# Revit family: Sanitary_Accessories_DURAVIT-AG_Starck-T-Toothbrush-cup-65x98x173-mm-009
name_source: partatom
category: Generic Models
revit_build: Autodesk Revit 2018 (Build: 20180329_1100(x64)
units: mm (PartAtom-declared; Revit-internal decimal feet)

## family parameters
Can host rebar = No
Cut with Voids When Loaded = No
Host = Face
OmniClass Number = 23.31.25.00
OmniClass Title = Toilet and Bath Specialties
Part Type = Normal
Room Calculation Point = No
Round Connector Dimension = Use Diameter
Shared = No

## types (2) — shared parameters
BIMobject category = Bathroom Accessories
Default Elevation = 1219 mm
Design country = Germany
ETIM classification = EC010556 | Toothbrush holder
Edition number = 1
IFC Classification = Furnishing Element
Installation instructions = https://pro.duravit.com
Manufacturer = Duravit
Manufacturer country = Germany
Manufacturer name = DURAVIT AG
Masterformat 2014 Code = 01 52 19
Masterformat 2014 Description = Sanitary Facilities
Material main = Brass
Material secondary = Glass frosted
Model = Starck T Toothbrush cup 65x98x173 mm - 009931
OmniClass Code = 23-31 25 00
OmniClass Description = Toilet and Bath Specialties
Product Guid = da395057-32e6-4f7c-89dd-928aacf0623f
Product SKU = Starck-T-Toothbrush-cup-65x98x173-mm-009931
Product certification = https://pro.duravit.com
Product data url = https://bimobject.com
Product family = Starck T
Product group = Toothbrush cup
Product name = Starck T Toothbrush cup 65x98x173 mm - 009931
Product url = https://pro.duravit.com
QR code = https://bimobject.com
Scondary material = Duravit - Glass - Frosted
Technical description = https://pro.duravit.com
UNSPSC Code = 301815
URL = https://www.duravit.com
Uniclass 2015 Code = Pr_40_20
Uniclass 2015 Name = Sanitary fittings and accessories
Uniformat II Code = E2010
Uniformat II Description = Fixed Furnishings
Weight Net (Kg) = 0.6
Youtube clip = https://pro.duravit.com

## per-type parameters (varying)
| type | Description | Main material |
| 10 - Chrome | Duravit Starck T Toothbrush cup Chrome 65x98x173 mm - 0099311000 | Duravit - Metal - 10 - Chrome |
| 46 - Black Matt | Duravit Starck T Toothbrush cup Black Matt 65x98x173 mm - 0099314600 | Duravit - Metal - 46 - Black Matt |

## geometry (parser evidence)
native form markers: Sweep x3
no freeform markers — native parametric forms only
